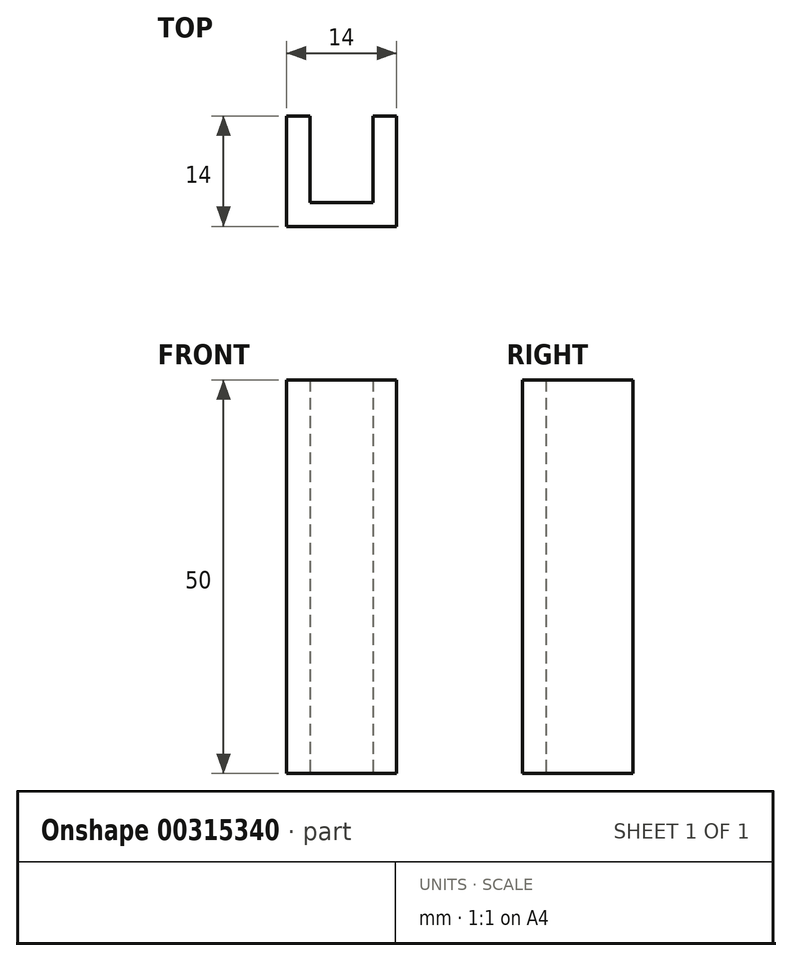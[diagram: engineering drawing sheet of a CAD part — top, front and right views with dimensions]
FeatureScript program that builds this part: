
annotation { "Feature Type Name" : "Feature", "Feature Type Description" : "" }
export const myFeature = defineFeature(function(context is Context, id is Id, definition is map)
    precondition{}
    {
        {
            var Q0;
            Q0=qCreatedBy(makeId("Top.planeOp"),FACE);
            var sketch = newSketch(context, id + "F0", { "sketchPlane" : qUnion([Q0])});
            skPoint(sketch, "E0", {"position": v(-8.32, 6.59) * mm});
            skPoint(sketch, "E1", {"position": v(-5.32, 6.59) * mm});
            skPoint(sketch, "E2", {"position": v(-5.32, -4.41) * mm});
            skPoint(sketch, "E3", {"position": v(2.68, -4.41) * mm});
            skPoint(sketch, "E4", {"position": v(2.68, 6.59) * mm});
            skPoint(sketch, "E5", {"position": v(5.68, 6.59) * mm});
            skPoint(sketch, "E6", {"position": v(5.37, -7.41) * mm});
            skPoint(sketch, "E7", {"position": v(-8.4, -7.41) * mm});
            skLineSegment(sketch, "E8", {"start": v(-8.32, 6.59) * mm, "end": v(-8.32, -7.41) * mm});
            skLineSegment(sketch, "E9", {"start": v(-8.32, -7.41) * mm, "end": v(5.68, -7.41) * mm});
            skLineSegment(sketch, "E10", {"start": v(5.68, -7.41) * mm, "end": v(5.68, 6.59) * mm});
            skLineSegment(sketch, "E11", {"start": v(2.68, 6.59) * mm, "end": v(2.68, -4.41) * mm});
            skLineSegment(sketch, "E12", {"start": v(2.68, 6.59) * mm, "end": v(5.68, 6.59) * mm});
            skLineSegment(sketch, "E13", {"start": v(2.68, -4.41) * mm, "end": v(-5.32, -4.41) * mm});
            skLineSegment(sketch, "E14", {"start": v(-5.32, -4.41) * mm, "end": v(-5.32, 6.59) * mm});
            skLineSegment(sketch, "E15", {"start": v(-5.32, 6.59) * mm, "end": v(-8.32, 6.59) * mm});
            skSolve(sketch);
        }
        {
            var Q0;
            Q0=makeQuery(id+"F0.imprint","IMPRINT",FACE,{"disambiguationData":[TD([[makeQuery(id+"F0.imprint","IMPRINT",EDGE,{"derivedFrom":sQuery(id+"F0.wireOp",EDGE,"E8")}),1.0]])]});
            extrude(context, id + "F1", {"entities" : qUnion([Q0]), "depth" : 50 * mm});
        }
    });
